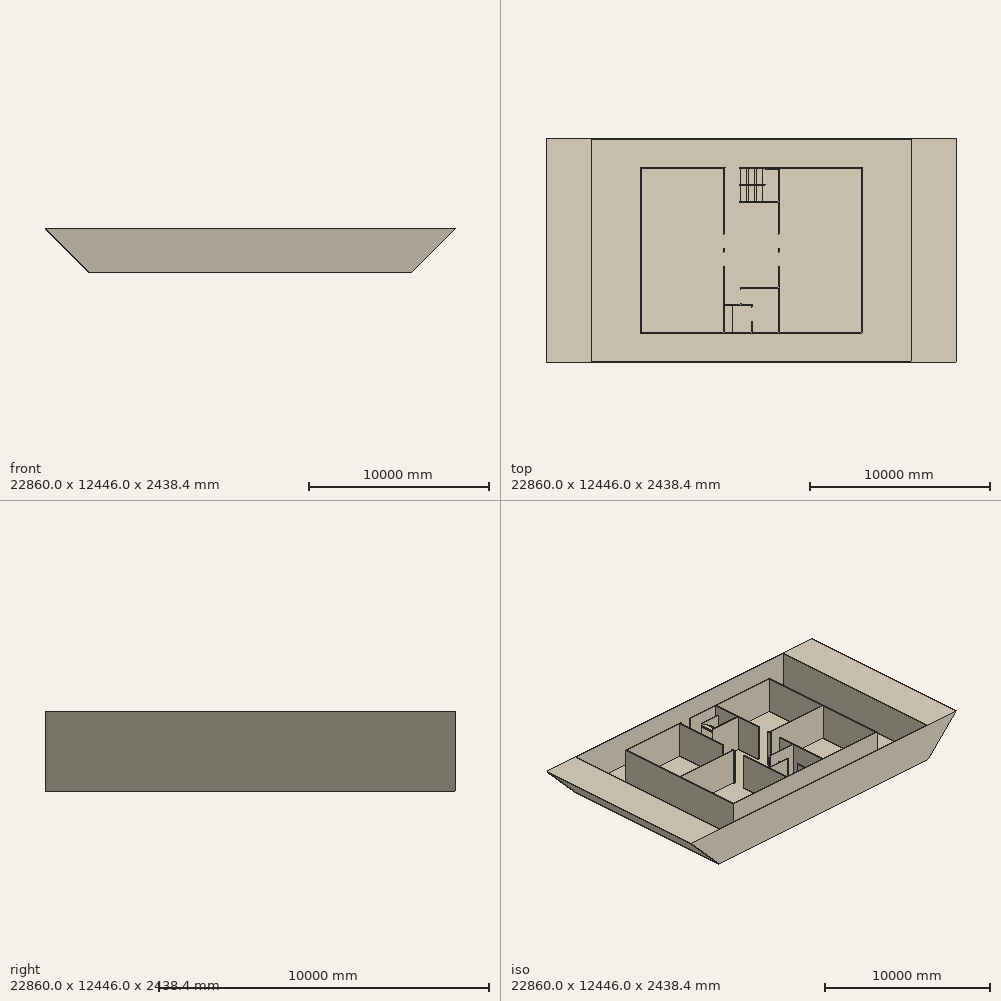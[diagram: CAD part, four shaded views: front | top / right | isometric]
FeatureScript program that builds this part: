
annotation { "Feature Type Name" : "Feature", "Feature Type Description" : "" }
export const myFeature = defineFeature(function(context is Context, id is Id, definition is map)
    precondition{}
    {
        {
            var Q0;
            Q0=qCreatedBy(makeId("Top.planeOp"),FACE);
            var sketch = newSketch(context, id + "F0", { "sketchPlane" : qUnion([Q0])});
            skLineSegment(sketch, "E0.bottom", {"start": v(-95.25, -51.86) * mm, "end": v(95.25, -51.86) * mm});
            skLineSegment(sketch, "E0.top", {"start": v(-95.25, 51.86) * mm, "end": v(95.25, 51.86) * mm});
            skLineSegment(sketch, "E0.left", {"start": v(-95.25, -51.86) * mm, "end": v(-95.25, 51.86) * mm});
            skLineSegment(sketch, "E0.right", {"start": v(95.25, -51.86) * mm, "end": v(95.25, 51.86) * mm});
            skPoint(sketch, "E0.middle", {"position": v(0, 0) * mm});
            skSolve(sketch);
        }
        {
            var Q0;
            Q0=makeQuery(id+"F0.imprint","IMPRINT",FACE,{"disambiguationData":[TD([[makeQuery(id+"F0.imprint","IMPRINT",EDGE,{"derivedFrom":sQuery(id+"F0.wireOp",EDGE,"E0.bottom")}),1.0]])]});
            extrude(context, id + "F1", {"entities" : qUnion([Q0]), "depth" : 20.32 * mm});
        }
        {
            var Q0;
            Q0=makeQuery(id+"F1.opExtrude","CAP_EDGE",EDGE,{"disambiguationData":[OSD([sQuery(id+"F0.wireOp",EDGE,"E0.right")])],"isStart":true});
            var Q1;
            Q1=makeQuery(id+"F1.opExtrude","CAP_EDGE",EDGE,{"disambiguationData":[OSD([sQuery(id+"F0.wireOp",EDGE,"E0.left")])],"isStart":true});
            chamfer(context, id + "F2", {"entities" : qUnion([Q0, Q1]), "width" : 20.32 * mm, "tangentPropagation" : true});
        }
        {
            var Q0;
            Q0=makeQuery(id+"F1.opExtrude","CAP_FACE",FACE,{"disambiguationData":[OSD([sQuery(id+"F0.wireOp",EDGE,"E0.bottom"),sQuery(id+"F0.wireOp",EDGE,"E0.top"),sQuery(id+"F0.wireOp",EDGE,"E0.left"),sQuery(id+"F0.wireOp",EDGE,"E0.right")])],"isStart":false});
            var sketch = newSketch(context, id + "F3", { "sketchPlane" : qUnion([Q0])});
            skLineSegment(sketch, "E1.bottom", {"start": v(-51.65, -38.73) * mm, "end": v(51.65, -38.73) * mm});
            skLineSegment(sketch, "E1.top", {"start": v(-51.65, 38.73) * mm, "end": v(51.65, 38.73) * mm});
            skLineSegment(sketch, "E1.left", {"start": v(-51.65, -38.73) * mm, "end": v(-51.65, 38.73) * mm});
            skLineSegment(sketch, "E1.right", {"start": v(51.65, -38.73) * mm, "end": v(51.65, 38.74) * mm});
            skPoint(sketch, "E1.middle", {"position": v(0, 0) * mm});
            skLineSegment(sketch, "E2.bottom", {"start": v(-74.5, -51.44) * mm, "end": v(74.5, -51.44) * mm});
            skLineSegment(sketch, "E2.top", {"start": v(-74.5, 51.44) * mm, "end": v(74.5, 51.44) * mm});
            skLineSegment(sketch, "E2.left", {"start": v(-74.5, -51.44) * mm, "end": v(-74.5, 51.44) * mm});
            skLineSegment(sketch, "E2.right", {"start": v(74.5, -51.44) * mm, "end": v(74.5, 51.44) * mm});
            skLineSegment(sketch, "E3", {"start": v(-74.93, 51.86) * mm, "end": v(-74.93, -51.86) * mm});
            skLineSegment(sketch, "E4", {"start": v(74.93, 51.86) * mm, "end": v(74.93, -51.86) * mm});
            skLineSegment(sketch, "E5.bottom", {"start": v(-51.22, 38.31) * mm, "end": v(-13.12, 38.31) * mm});
            skLineSegment(sketch, "E5.top", {"start": v(-51.22, 0.21) * mm, "end": v(-13.12, 0.21) * mm});
            skLineSegment(sketch, "E5.left", {"start": v(-51.22, 38.31) * mm, "end": v(-51.22, 0.21) * mm});
            skLineSegment(sketch, "E5.right", {"start": v(-13.12, 38.31) * mm, "end": v(-13.12, 0.21) * mm});
            skLineSegment(sketch, "E6.bottom", {"start": v(-51.22, -0.21) * mm, "end": v(-13.12, -0.21) * mm});
            skLineSegment(sketch, "E6.top", {"start": v(-51.22, -38.31) * mm, "end": v(-13.12, -38.31) * mm});
            skLineSegment(sketch, "E6.left", {"start": v(-51.22, -0.21) * mm, "end": v(-51.22, -38.31) * mm});
            skLineSegment(sketch, "E6.right", {"start": v(-13.12, -0.21) * mm, "end": v(-13.12, -38.31) * mm});
            skLineSegment(sketch, "E7.bottom", {"start": v(13.12, 38.31) * mm, "end": v(51.22, 38.31) * mm});
            skLineSegment(sketch, "E7.top", {"start": v(13.12, 0.21) * mm, "end": v(51.22, 0.21) * mm});
            skLineSegment(sketch, "E7.left", {"start": v(13.12, 38.31) * mm, "end": v(13.12, 0.21) * mm});
            skLineSegment(sketch, "E7.right", {"start": v(51.22, 38.31) * mm, "end": v(51.22, 0.21) * mm});
            skLineSegment(sketch, "E8.bottom", {"start": v(13.12, -0.21) * mm, "end": v(51.22, -0.21) * mm});
            skLineSegment(sketch, "E8.top", {"start": v(13.12, -38.31) * mm, "end": v(51.22, -38.31) * mm});
            skLineSegment(sketch, "E8.left", {"start": v(13.12, -0.21) * mm, "end": v(13.12, -38.31) * mm});
            skLineSegment(sketch, "E8.right", {"start": v(51.22, -0.21) * mm, "end": v(51.22, -38.31) * mm});
            skLineSegment(sketch, "E9", {"start": v(-12.7, 38.73) * mm, "end": v(-12.7, -38.74) * mm});
            skLineSegment(sketch, "E10", {"start": v(12.7, 38.73) * mm, "end": v(12.7, -38.74) * mm});
            skLineSegment(sketch, "E11", {"start": v(-12.7, 38.31) * mm, "end": v(12.7, 38.31) * mm});
            skLineSegment(sketch, "E12", {"start": v(12.7, -38.31) * mm, "end": v(-12.7, -38.31) * mm});
            skLineSegment(sketch, "E13", {"start": v(-12.7, -25.61) * mm, "end": v(0, -25.61) * mm});
            skLineSegment(sketch, "E14", {"start": v(-12.7, -17.14) * mm, "end": v(12.7, -17.14) * mm});
            skLineSegment(sketch, "E15", {"start": v(-12.7, -17.57) * mm, "end": v(12.7, -17.57) * mm});
            skLineSegment(sketch, "E16", {"start": v(-12.7, -25.19) * mm, "end": v(0, -25.19) * mm});
            skLineSegment(sketch, "E17", {"start": v(0, -25.19) * mm, "end": v(0, -25.61) * mm});
            skLineSegment(sketch, "E18", {"start": v(0, -25.61) * mm, "end": v(0, -38.31) * mm});
            skLineSegment(sketch, "E19", {"start": v(0.42, -38.31) * mm, "end": v(0.42, -25.19) * mm});
            skLineSegment(sketch, "E20", {"start": v(0.42, -25.19) * mm, "end": v(0, -25.19) * mm});
            skLineSegment(sketch, "E21", {"start": v(-5.08, -17.14) * mm, "end": v(-5.08, -25.19) * mm});
            skLineSegment(sketch, "E22", {"start": v(-4.66, -17.57) * mm, "end": v(-4.66, -25.19) * mm});
            skSolve(sketch);
        }
        {
            var Q0;
            {var subQ1=sQuery(id+"F3.wireOp",EDGE,"E1.left");Q0=makeQuery(id+"F3.imprint","IMPRINT",FACE,{"disambiguationData":[TD([[makeQuery(id+"F3.imprint","IMPRINT",EDGE,{"derivedFrom":subQ1}),1.0]])]});}
            var Q1;
            Q1=makeQuery(id+"F3.imprint","IMPRINT",FACE,{"disambiguationData":[TD([[makeQuery(id+"F3.imprint","IMPRINT",EDGE,{"derivedFrom":sQuery(id+"F3.wireOp",EDGE,"E5.bottom")}),-1.0]])]});
            var Q2;
            Q2=makeQuery(id+"F3.imprint","IMPRINT",FACE,{"disambiguationData":[TD([[makeQuery(id+"F3.imprint","IMPRINT",EDGE,{"derivedFrom":sQuery(id+"F3.wireOp",EDGE,"E6.bottom")}),-1.0]])]});
            var Q3;
            {var subQ0=sQuery(id+"F3.wireOp",EDGE,"E11");Q3=makeQuery(id+"F3.imprint","IMPRINT",FACE,{"disambiguationData":[TD([[makeQuery(id+"F3.imprint","IMPRINT",EDGE,{"derivedFrom":subQ0}),-1.0]])]});}
            var Q4;
            Q4=makeQuery(id+"F3.imprint","IMPRINT",FACE,{"disambiguationData":[TD([[makeQuery(id+"F3.imprint","IMPRINT",EDGE,{"derivedFrom":sQuery(id+"F3.wireOp",EDGE,"E7.bottom")}),-1.0]])]});
            var Q5;
            Q5=makeQuery(id+"F3.imprint","IMPRINT",FACE,{"disambiguationData":[TD([[makeQuery(id+"F3.imprint","IMPRINT",EDGE,{"derivedFrom":sQuery(id+"F3.wireOp",EDGE,"E8.bottom")}),-1.0]])]});
            var Q6;
            {var subQ0=sQuery(id+"F3.wireOp",EDGE,"E14");var subQ1=sQuery(id+"F3.wireOp",EDGE,"E9");var subQ2=makeQuery(id+"F3.imprint","INTERSECT",VERTEX,{"derivedFrom":[subQ1,subQ0]});Q6=makeQuery(id+"F3.imprint","IMPRINT",FACE,{"disambiguationData":[TD([[makeQuery(id+"F3.imprint","IMPRINT",EDGE,{"disambiguationData":[TD([[subQ2,-1.0]])],"derivedFrom":subQ1}),1.0]])]});}
            var Q7;
            {var subQ0=sQuery(id+"F3.wireOp",EDGE,"E15");var subQ1=sQuery(id+"F3.wireOp",EDGE,"E9");var subQ2=makeQuery(id+"F3.imprint","INTERSECT",VERTEX,{"derivedFrom":[subQ1,subQ0]});Q7=makeQuery(id+"F3.imprint","IMPRINT",FACE,{"disambiguationData":[TD([[makeQuery(id+"F3.imprint","IMPRINT",EDGE,{"disambiguationData":[TD([[subQ2,-1.0]])],"derivedFrom":subQ1}),1.0]])]});}
            var Q8;
            {var subQ3=sQuery(id+"F3.wireOp",EDGE,"E13");Q8=makeQuery(id+"F3.imprint","IMPRINT",FACE,{"disambiguationData":[TD([[makeQuery(id+"F3.imprint","IMPRINT",EDGE,{"derivedFrom":subQ3}),-1.0]])]});}
            var Q9;
            {var subQ7=sQuery(id+"F3.wireOp",EDGE,"E19");Q9=makeQuery(id+"F3.imprint","IMPRINT",FACE,{"disambiguationData":[TD([[makeQuery(id+"F3.imprint","IMPRINT",EDGE,{"derivedFrom":subQ7}),-1.0]])]});}
            extrude(context, id + "F4", {"entities" : qUnion([Q0, Q1, Q2, Q3, Q4, Q5, Q6, Q7, Q8, Q9]), "operationType" : NewBodyOperationType.REMOVE, "oppositeDirection" : true, "depth" : 19.05 * mm});
        }
        {
            var Q0;
            Q0=makeQuery(id+"F4.boolean.opBoolean","COPY",FACE,{"derivedFrom":makeQuery(id+"F4.opExtrude","CAP_FACE",FACE,{"disambiguationData":[OSD([sQuery(id+"F3.wireOp",EDGE,"E8.bottom"),sQuery(id+"F3.wireOp",EDGE,"E8.top"),sQuery(id+"F3.wireOp",EDGE,"E8.left"),sQuery(id+"F3.wireOp",EDGE,"E8.right")])],"isStart":false})});
            var sketch = newSketch(context, id + "F5", { "sketchPlane" : qUnion([Q0])});
            skLineSegment(sketch, "E23.bottom", {"start": v(-14.93, -1.06) * mm, "end": v(-4.43, -1.06) * mm});
            skLineSegment(sketch, "E23.top", {"start": v(-14.93, -7.4) * mm, "end": v(-4.43, -7.4) * mm});
            skLineSegment(sketch, "E23.left", {"start": v(-14.93, -1.06) * mm, "end": v(-14.93, -7.4) * mm});
            skLineSegment(sketch, "E23.right", {"start": v(-4.43, -1.06) * mm, "end": v(-4.43, -7.4) * mm});
            skLineSegment(sketch, "E24.bottom", {"start": v(4.64, -1.06) * mm, "end": v(13.64, -1.06) * mm});
            skLineSegment(sketch, "E24.top", {"start": v(4.64, -7.4) * mm, "end": v(13.64, -7.4) * mm});
            skLineSegment(sketch, "E24.left", {"start": v(4.64, -1.06) * mm, "end": v(4.64, -7.4) * mm});
            skLineSegment(sketch, "E24.right", {"start": v(13.64, -1.06) * mm, "end": v(13.64, -7.4) * mm});
            skLineSegment(sketch, "E25.bottom", {"start": v(13.6, 1.06) * mm, "end": v(2.84, 1.06) * mm});
            skLineSegment(sketch, "E25.top", {"start": v(13.6, 7.4) * mm, "end": v(2.84, 7.4) * mm});
            skLineSegment(sketch, "E25.left", {"start": v(13.6, 1.06) * mm, "end": v(13.6, 7.4) * mm});
            skLineSegment(sketch, "E25.right", {"start": v(2.84, 1.06) * mm, "end": v(2.84, 7.4) * mm});
            skLineSegment(sketch, "E26.bottom", {"start": v(-13.48, 7.4) * mm, "end": v(-3.4, 7.4) * mm});
            skLineSegment(sketch, "E26.top", {"start": v(-13.48, 1.06) * mm, "end": v(-3.4, 1.06) * mm});
            skLineSegment(sketch, "E26.left", {"start": v(-13.48, 7.4) * mm, "end": v(-13.48, 1.06) * mm});
            skLineSegment(sketch, "E26.right", {"start": v(-3.4, 7.4) * mm, "end": v(-3.4, 1.06) * mm});
            skLineSegment(sketch, "E27.bottom", {"start": v(-8.3, -18.2) * mm, "end": v(0, -18.2) * mm});
            skLineSegment(sketch, "E27.top", {"start": v(-8.3, -24.55) * mm, "end": v(0, -24.55) * mm});
            skLineSegment(sketch, "E27.left", {"start": v(-8.3, -18.2) * mm, "end": v(-8.3, -24.55) * mm});
            skLineSegment(sketch, "E27.right", {"start": v(0, -18.2) * mm, "end": v(0, -24.55) * mm});
            skLineSegment(sketch, "E28.bottom", {"start": v(-11.85, 42.33) * mm, "end": v(-5.5, 42.33) * mm});
            skLineSegment(sketch, "E28.top", {"start": v(-11.85, 34.48) * mm, "end": v(-5.5, 34.48) * mm});
            skLineSegment(sketch, "E28.left", {"start": v(-11.85, 42.33) * mm, "end": v(-11.85, 34.48) * mm});
            skLineSegment(sketch, "E28.right", {"start": v(-5.5, 42.33) * mm, "end": v(-5.5, 34.48) * mm});
            skLineSegment(sketch, "E29.bottom", {"start": v(-2.51, -26.46) * mm, "end": v(3, -26.46) * mm});
            skLineSegment(sketch, "E29.top", {"start": v(-2.51, -32.8) * mm, "end": v(3, -32.8) * mm});
            skLineSegment(sketch, "E29.left", {"start": v(-2.51, -26.46) * mm, "end": v(-2.51, -32.8) * mm});
            skLineSegment(sketch, "E29.right", {"start": v(3, -26.46) * mm, "end": v(3, -32.8) * mm});
            skSolve(sketch);
        }
        {
            var Q0;
            Q0 = qSketchRegion(id + "F5", true);
            extrude(context, id + "F6", {"entities" : qUnion([Q0]), "operationType" : NewBodyOperationType.REMOVE, "depth" : 25.4 * mm});
        }
        {
            var Q0;
            {var subQ0=sQuery(id+"F3.wireOp",EDGE,"E16");var subQ1=sQuery(id+"F3.wireOp",EDGE,"E10");Q0=makeQuery(id+"F6.boolean.opBoolean","MERGE",FACE,{"derivedFrom":[makeQuery(id+"F4.boolean.opBoolean","COPY",FACE,{"derivedFrom":makeQuery(id+"F4.opExtrude","CAP_FACE",FACE,{"disambiguationData":[OSD([sQuery(id+"F3.wireOp",EDGE,"E1.bottom"),sQuery(id+"F3.wireOp",EDGE,"E1.top"),sQuery(id+"F3.wireOp",EDGE,"E1.left"),sQuery(id+"F3.wireOp",EDGE,"E1.right"),sQuery(id+"F3.wireOp",EDGE,"E2.bottom"),sQuery(id+"F3.wireOp",EDGE,"E2.top"),sQuery(id+"F3.wireOp",EDGE,"E2.left"),sQuery(id+"F3.wireOp",EDGE,"E2.right")])],"isStart":false})}),makeQuery(id+"F4.boolean.opBoolean","COPY",FACE,{"derivedFrom":makeQuery(id+"F4.opExtrude","CAP_FACE",FACE,{"disambiguationData":[OSD([sQuery(id+"F3.wireOp",EDGE,"E5.bottom"),sQuery(id+"F3.wireOp",EDGE,"E5.top"),sQuery(id+"F3.wireOp",EDGE,"E5.left"),sQuery(id+"F3.wireOp",EDGE,"E5.right")])],"isStart":false})}),makeQuery(id+"F4.boolean.opBoolean","COPY",FACE,{"derivedFrom":makeQuery(id+"F4.opExtrude","CAP_FACE",FACE,{"disambiguationData":[OSD([sQuery(id+"F3.wireOp",EDGE,"E6.bottom"),sQuery(id+"F3.wireOp",EDGE,"E6.top"),sQuery(id+"F3.wireOp",EDGE,"E6.left"),sQuery(id+"F3.wireOp",EDGE,"E6.right")])],"isStart":false})}),makeQuery(id+"F4.boolean.opBoolean","COPY",FACE,{"derivedFrom":makeQuery(id+"F4.opExtrude","CAP_FACE",FACE,{"disambiguationData":[OSD([sQuery(id+"F3.wireOp",EDGE,"E7.bottom"),sQuery(id+"F3.wireOp",EDGE,"E7.top"),sQuery(id+"F3.wireOp",EDGE,"E7.left"),sQuery(id+"F3.wireOp",EDGE,"E7.right")])],"isStart":false})}),makeQuery(id+"F4.boolean.opBoolean","COPY",FACE,{"derivedFrom":makeQuery(id+"F4.opExtrude","CAP_FACE",FACE,{"disambiguationData":[OSD([sQuery(id+"F3.wireOp",EDGE,"E8.bottom"),sQuery(id+"F3.wireOp",EDGE,"E8.top"),sQuery(id+"F3.wireOp",EDGE,"E8.left"),sQuery(id+"F3.wireOp",EDGE,"E8.right")])],"isStart":false})}),makeQuery(id+"F4.boolean.opBoolean","COPY",FACE,{"derivedFrom":makeQuery(id+"F4.opExtrude","CAP_FACE",FACE,{"disambiguationData":[OSD([sQuery(id+"F3.wireOp",EDGE,"E9"),subQ1,sQuery(id+"F3.wireOp",EDGE,"E11"),sQuery(id+"F3.wireOp",EDGE,"E14"),subQ0,sQuery(id+"F3.wireOp",EDGE,"E21")])],"isStart":false})}),makeQuery(id+"F4.boolean.opBoolean","COPY",FACE,{"derivedFrom":makeQuery(id+"F4.opExtrude","CAP_FACE",FACE,{"disambiguationData":[OSD([subQ1,sQuery(id+"F3.wireOp",EDGE,"E12"),sQuery(id+"F3.wireOp",EDGE,"E15"),subQ0,sQuery(id+"F3.wireOp",EDGE,"E19"),sQuery(id+"F3.wireOp",EDGE,"E20"),sQuery(id+"F3.wireOp",EDGE,"E22")])],"isStart":false})}),makeQuery(id+"F6.opExtrude","CAP_FACE",FACE,{"disambiguationData":[OSD([sQuery(id+"F5.wireOp",EDGE,"E23.bottom"),sQuery(id+"F5.wireOp",EDGE,"E23.top"),sQuery(id+"F5.wireOp",EDGE,"E23.left"),sQuery(id+"F5.wireOp",EDGE,"E23.right")])],"isStart":true}),makeQuery(id+"F6.opExtrude","CAP_FACE",FACE,{"disambiguationData":[OSD([sQuery(id+"F5.wireOp",EDGE,"E24.bottom"),sQuery(id+"F5.wireOp",EDGE,"E24.top"),sQuery(id+"F5.wireOp",EDGE,"E24.left"),sQuery(id+"F5.wireOp",EDGE,"E24.right")])],"isStart":true}),makeQuery(id+"F6.opExtrude","CAP_FACE",FACE,{"disambiguationData":[OSD([sQuery(id+"F5.wireOp",EDGE,"E25.bottom"),sQuery(id+"F5.wireOp",EDGE,"E25.top"),sQuery(id+"F5.wireOp",EDGE,"E25.left"),sQuery(id+"F5.wireOp",EDGE,"E25.right")])],"isStart":true}),makeQuery(id+"F6.opExtrude","CAP_FACE",FACE,{"disambiguationData":[OSD([sQuery(id+"F5.wireOp",EDGE,"E26.bottom"),sQuery(id+"F5.wireOp",EDGE,"E26.top"),sQuery(id+"F5.wireOp",EDGE,"E26.left"),sQuery(id+"F5.wireOp",EDGE,"E26.right")])],"isStart":true}),makeQuery(id+"F6.opExtrude","CAP_FACE",FACE,{"disambiguationData":[OSD([sQuery(id+"F5.wireOp",EDGE,"E27.bottom"),sQuery(id+"F5.wireOp",EDGE,"E27.top"),sQuery(id+"F5.wireOp",EDGE,"E27.left"),sQuery(id+"F5.wireOp",EDGE,"E27.right")])],"isStart":true}),makeQuery(id+"F6.opExtrude","CAP_FACE",FACE,{"disambiguationData":[OSD([sQuery(id+"F5.wireOp",EDGE,"E28.bottom"),sQuery(id+"F5.wireOp",EDGE,"E28.top"),sQuery(id+"F5.wireOp",EDGE,"E28.left"),sQuery(id+"F5.wireOp",EDGE,"E28.right")])],"isStart":true})]});}
            var sketch = newSketch(context, id + "F7", { "sketchPlane" : qUnion([Q0])});
            skLineSegment(sketch, "E30", {"start": v(12.7, 30.7) * mm, "end": v(-5.5, 30.7) * mm});
            skLineSegment(sketch, "E31", {"start": v(12.7, 30.27) * mm, "end": v(-5.5, 30.27) * mm});
            skLineSegment(sketch, "E32", {"start": v(-5.5, 30.27) * mm, "end": v(-5.5, 30.7) * mm});
            skLineSegment(sketch, "E33", {"start": v(6.35, 30.7) * mm, "end": v(6.35, 30.27) * mm});
            skSolve(sketch);
        }
        {
            var Q0;
            {var subQ0=sQuery(id+"F7.wireOp",EDGE,"E32");Q0=makeQuery(id+"F7.imprint","IMPRINT",FACE,{"disambiguationData":[TD([[makeQuery(id+"F7.imprint","IMPRINT",EDGE,{"derivedFrom":subQ0}),-1.0]])]});}
            extrude(context, id + "F8", {"entities" : qUnion([Q0]), "operationType" : NewBodyOperationType.ADD, "depth" : 19.05 * mm});
        }
        {
            var Q0;
            Q0=makeQuery(id+"F4.boolean.opBoolean","COPY",FACE,{"derivedFrom":makeQuery(id+"F4.opExtrude","SWEPT_FACE",FACE,{"disambiguationData":[OSD([sQuery(id+"F3.wireOp",EDGE,"E11")])]})});
            var sketch = newSketch(context, id + "F9", { "sketchPlane" : qUnion([Q0])});
            skLineSegment(sketch, "E34.bottom", {"start": v(-5.08, 3.81) * mm, "end": v(-2.54, 3.81) * mm});
            skLineSegment(sketch, "E34.top", {"start": v(-5.08, 2.96) * mm, "end": v(-2.54, 2.96) * mm});
            skLineSegment(sketch, "E34.left", {"start": v(-5.08, 3.81) * mm, "end": v(-5.08, 2.96) * mm});
            skLineSegment(sketch, "E34.right", {"start": v(-2.54, 3.81) * mm, "end": v(-2.54, 2.96) * mm});
            skLineSegment(sketch, "E35.bottom", {"start": v(2.54, 8.9) * mm, "end": v(5.08, 8.9) * mm});
            skLineSegment(sketch, "E35.top", {"start": v(2.54, 8.04) * mm, "end": v(5.08, 8.04) * mm});
            skLineSegment(sketch, "E35.left", {"start": v(2.54, 8.9) * mm, "end": v(2.54, 8.04) * mm});
            skLineSegment(sketch, "E35.right", {"start": v(5.08, 8.9) * mm, "end": v(5.08, 8.04) * mm});
            skLineSegment(sketch, "E36.bottom", {"start": v(6.35, 11.43) * mm, "end": v(8.9, 11.43) * mm});
            skLineSegment(sketch, "E36.top", {"start": v(6.35, 10.58) * mm, "end": v(8.9, 10.58) * mm});
            skLineSegment(sketch, "E36.left", {"start": v(6.35, 11.43) * mm, "end": v(6.35, 10.58) * mm});
            skLineSegment(sketch, "E36.right", {"start": v(8.9, 11.43) * mm, "end": v(8.9, 10.58) * mm});
            skLineSegment(sketch, "E37.bottom", {"start": v(-1.27, 6.35) * mm, "end": v(1.27, 6.35) * mm});
            skLineSegment(sketch, "E37.top", {"start": v(-1.27, 5.5) * mm, "end": v(1.27, 5.5) * mm});
            skLineSegment(sketch, "E37.left", {"start": v(-1.27, 6.35) * mm, "end": v(-1.27, 5.5) * mm});
            skLineSegment(sketch, "E37.right", {"start": v(1.27, 6.35) * mm, "end": v(1.27, 5.5) * mm});
            skLineSegment(sketch, "E38.bottom", {"start": v(8.9, 11.43) * mm, "end": v(12.7, 11.43) * mm});
            skLineSegment(sketch, "E38.top", {"start": v(8.9, 10.58) * mm, "end": v(12.7, 10.58) * mm});
            skLineSegment(sketch, "E38.right", {"start": v(12.7, 11.43) * mm, "end": v(12.7, 10.58) * mm});
            skSolve(sketch);
        }
        {
            var Q0;
            Q0=makeQuery(id+"F9.imprint","IMPRINT",FACE,{"disambiguationData":[TD([[makeQuery(id+"F9.imprint","IMPRINT",EDGE,{"derivedFrom":sQuery(id+"F9.wireOp",EDGE,"E34.bottom")}),-1.0]])]});
            var Q1;
            Q1=makeQuery(id+"F9.imprint","IMPRINT",FACE,{"disambiguationData":[TD([[makeQuery(id+"F9.imprint","IMPRINT",EDGE,{"derivedFrom":sQuery(id+"F9.wireOp",EDGE,"E37.bottom")}),-1.0]])]});
            var Q2;
            Q2=makeQuery(id+"F9.imprint","IMPRINT",FACE,{"disambiguationData":[TD([[makeQuery(id+"F9.imprint","IMPRINT",EDGE,{"derivedFrom":sQuery(id+"F9.wireOp",EDGE,"E35.bottom")}),-1.0]])]});
            extrude(context, id + "F10", {"entities" : qUnion([Q0, Q1, Q2]), "operationType" : NewBodyOperationType.ADD, "depth" : 7.62 * mm});
        }
        {
            var Q0;
            Q0=makeQuery(id+"F9.imprint","IMPRINT",FACE,{"disambiguationData":[TD([[makeQuery(id+"F9.imprint","IMPRINT",EDGE,{"derivedFrom":sQuery(id+"F9.wireOp",EDGE,"E36.bottom")}),-1.0]])]});
            var Q1;
            Q1=makeQuery(id+"F9.imprint","IMPRINT",FACE,{"disambiguationData":[TD([[makeQuery(id+"F9.imprint","IMPRINT",EDGE,{"derivedFrom":sQuery(id+"F9.wireOp",EDGE,"E38.bottom")}),-1.0]])]});
            extrude(context, id + "F11", {"entities" : qUnion([Q0, Q1]), "operationType" : NewBodyOperationType.ADD, "depth" : (.6 + (.1 / 6)) * mm});
        }
        {
            var Q0;
            {var subQ0=sQuery(id+"F3.wireOp",EDGE,"E16");var subQ1=sQuery(id+"F3.wireOp",EDGE,"E10");Q0=makeQuery(id+"F6.boolean.opBoolean","MERGE",FACE,{"derivedFrom":[makeQuery(id+"F4.boolean.opBoolean","COPY",FACE,{"derivedFrom":makeQuery(id+"F4.opExtrude","CAP_FACE",FACE,{"disambiguationData":[OSD([sQuery(id+"F3.wireOp",EDGE,"E1.bottom"),sQuery(id+"F3.wireOp",EDGE,"E1.top"),sQuery(id+"F3.wireOp",EDGE,"E1.left"),sQuery(id+"F3.wireOp",EDGE,"E1.right"),sQuery(id+"F3.wireOp",EDGE,"E2.bottom"),sQuery(id+"F3.wireOp",EDGE,"E2.top"),sQuery(id+"F3.wireOp",EDGE,"E2.left"),sQuery(id+"F3.wireOp",EDGE,"E2.right")])],"isStart":false})}),makeQuery(id+"F4.boolean.opBoolean","COPY",FACE,{"derivedFrom":makeQuery(id+"F4.opExtrude","CAP_FACE",FACE,{"disambiguationData":[OSD([sQuery(id+"F3.wireOp",EDGE,"E5.bottom"),sQuery(id+"F3.wireOp",EDGE,"E5.top"),sQuery(id+"F3.wireOp",EDGE,"E5.left"),sQuery(id+"F3.wireOp",EDGE,"E5.right")])],"isStart":false})}),makeQuery(id+"F4.boolean.opBoolean","COPY",FACE,{"derivedFrom":makeQuery(id+"F4.opExtrude","CAP_FACE",FACE,{"disambiguationData":[OSD([sQuery(id+"F3.wireOp",EDGE,"E6.bottom"),sQuery(id+"F3.wireOp",EDGE,"E6.top"),sQuery(id+"F3.wireOp",EDGE,"E6.left"),sQuery(id+"F3.wireOp",EDGE,"E6.right")])],"isStart":false})}),makeQuery(id+"F4.boolean.opBoolean","COPY",FACE,{"derivedFrom":makeQuery(id+"F4.opExtrude","CAP_FACE",FACE,{"disambiguationData":[OSD([sQuery(id+"F3.wireOp",EDGE,"E7.bottom"),sQuery(id+"F3.wireOp",EDGE,"E7.top"),sQuery(id+"F3.wireOp",EDGE,"E7.left"),sQuery(id+"F3.wireOp",EDGE,"E7.right")])],"isStart":false})}),makeQuery(id+"F4.boolean.opBoolean","COPY",FACE,{"derivedFrom":makeQuery(id+"F4.opExtrude","CAP_FACE",FACE,{"disambiguationData":[OSD([sQuery(id+"F3.wireOp",EDGE,"E8.bottom"),sQuery(id+"F3.wireOp",EDGE,"E8.top"),sQuery(id+"F3.wireOp",EDGE,"E8.left"),sQuery(id+"F3.wireOp",EDGE,"E8.right")])],"isStart":false})}),makeQuery(id+"F4.boolean.opBoolean","COPY",FACE,{"derivedFrom":makeQuery(id+"F4.opExtrude","CAP_FACE",FACE,{"disambiguationData":[OSD([sQuery(id+"F3.wireOp",EDGE,"E9"),subQ1,sQuery(id+"F3.wireOp",EDGE,"E11"),sQuery(id+"F3.wireOp",EDGE,"E14"),subQ0,sQuery(id+"F3.wireOp",EDGE,"E21")])],"isStart":false})}),makeQuery(id+"F4.boolean.opBoolean","COPY",FACE,{"derivedFrom":makeQuery(id+"F4.opExtrude","CAP_FACE",FACE,{"disambiguationData":[OSD([subQ1,sQuery(id+"F3.wireOp",EDGE,"E12"),sQuery(id+"F3.wireOp",EDGE,"E15"),subQ0,sQuery(id+"F3.wireOp",EDGE,"E19"),sQuery(id+"F3.wireOp",EDGE,"E20"),sQuery(id+"F3.wireOp",EDGE,"E22")])],"isStart":false})}),makeQuery(id+"F6.opExtrude","CAP_FACE",FACE,{"disambiguationData":[OSD([sQuery(id+"F5.wireOp",EDGE,"E23.bottom"),sQuery(id+"F5.wireOp",EDGE,"E23.top"),sQuery(id+"F5.wireOp",EDGE,"E23.left"),sQuery(id+"F5.wireOp",EDGE,"E23.right")])],"isStart":true}),makeQuery(id+"F6.opExtrude","CAP_FACE",FACE,{"disambiguationData":[OSD([sQuery(id+"F5.wireOp",EDGE,"E24.bottom"),sQuery(id+"F5.wireOp",EDGE,"E24.top"),sQuery(id+"F5.wireOp",EDGE,"E24.left"),sQuery(id+"F5.wireOp",EDGE,"E24.right")])],"isStart":true}),makeQuery(id+"F6.opExtrude","CAP_FACE",FACE,{"disambiguationData":[OSD([sQuery(id+"F5.wireOp",EDGE,"E25.bottom"),sQuery(id+"F5.wireOp",EDGE,"E25.top"),sQuery(id+"F5.wireOp",EDGE,"E25.left"),sQuery(id+"F5.wireOp",EDGE,"E25.right")])],"isStart":true}),makeQuery(id+"F6.opExtrude","CAP_FACE",FACE,{"disambiguationData":[OSD([sQuery(id+"F5.wireOp",EDGE,"E26.bottom"),sQuery(id+"F5.wireOp",EDGE,"E26.top"),sQuery(id+"F5.wireOp",EDGE,"E26.left"),sQuery(id+"F5.wireOp",EDGE,"E26.right")])],"isStart":true}),makeQuery(id+"F6.opExtrude","CAP_FACE",FACE,{"disambiguationData":[OSD([sQuery(id+"F5.wireOp",EDGE,"E27.bottom"),sQuery(id+"F5.wireOp",EDGE,"E27.top"),sQuery(id+"F5.wireOp",EDGE,"E27.left"),sQuery(id+"F5.wireOp",EDGE,"E27.right")])],"isStart":true}),makeQuery(id+"F6.opExtrude","CAP_FACE",FACE,{"disambiguationData":[OSD([sQuery(id+"F5.wireOp",EDGE,"E28.bottom"),sQuery(id+"F5.wireOp",EDGE,"E28.top"),sQuery(id+"F5.wireOp",EDGE,"E28.left"),sQuery(id+"F5.wireOp",EDGE,"E28.right")])],"isStart":true})]});}
            var sketch = newSketch(context, id + "F12", { "sketchPlane" : qUnion([Q0])});
            skLineSegment(sketch, "E39.bottom", {"start": v(12.7, 22.65) * mm, "end": v(-5.5, 22.65) * mm});
            skLineSegment(sketch, "E39.top", {"start": v(12.7, 22.22) * mm, "end": v(-5.5, 22.22) * mm});
            skLineSegment(sketch, "E39.left", {"start": v(12.7, 22.65) * mm, "end": v(12.7, 22.22) * mm});
            skLineSegment(sketch, "E39.right", {"start": v(-5.5, 22.65) * mm, "end": v(-5.5, 22.22) * mm});
            skSolve(sketch);
        }
        {
            var Q0;
            Q0 = qSketchRegion(id + "F12", true);
            extrude(context, id + "F13", {"entities" : qUnion([Q0]), "operationType" : NewBodyOperationType.ADD, "depth" : 19.05 * mm});
        }
        {
            var Q0;
            Q0=makeQuery(id+"F8.opExtrude","SWEPT_FACE",FACE,{"disambiguationData":[OSD([sQuery(id+"F7.wireOp",EDGE,"E31")])]});
            var sketch = newSketch(context, id + "F14", { "sketchPlane" : qUnion([Q0])});
            skLineSegment(sketch, "E40.bottom", {"start": v(-1.27, 16.51) * mm, "end": v(1.27, 16.51) * mm});
            skLineSegment(sketch, "E40.top", {"start": v(-1.27, 15.66) * mm, "end": v(1.27, 15.66) * mm});
            skLineSegment(sketch, "E40.left", {"start": v(-1.27, 16.51) * mm, "end": v(-1.27, 15.66) * mm});
            skLineSegment(sketch, "E40.right", {"start": v(1.27, 16.51) * mm, "end": v(1.27, 15.66) * mm});
            skLineSegment(sketch, "E41.bottom", {"start": v(5.08, 13.97) * mm, "end": v(2.54, 13.97) * mm});
            skLineSegment(sketch, "E41.top", {"start": v(5.08, 12.95) * mm, "end": v(2.54, 12.95) * mm});
            skLineSegment(sketch, "E41.left", {"start": v(5.08, 13.97) * mm, "end": v(5.08, 12.95) * mm});
            skLineSegment(sketch, "E41.right", {"start": v(2.54, 13.97) * mm, "end": v(2.54, 12.95) * mm});
            skLineSegment(sketch, "E42.bottom", {"start": v(-2.54, 19.05) * mm, "end": v(-5.08, 19.05) * mm});
            skLineSegment(sketch, "E42.top", {"start": v(-2.54, 18.2) * mm, "end": v(-5.08, 18.2) * mm});
            skLineSegment(sketch, "E42.left", {"start": v(-2.54, 19.05) * mm, "end": v(-2.54, 18.2) * mm});
            skLineSegment(sketch, "E42.right", {"start": v(-5.08, 19.05) * mm, "end": v(-5.08, 18.2) * mm});
            skSolve(sketch);
        }
        {
            var Q0;
            Q0 = qSketchRegion(id + "F14", true);
            extrude(context, id + "F15", {"entities" : qUnion([Q0]), "operationType" : NewBodyOperationType.ADD, "depth" : 7.62 * mm});
        }
        {
            var Q0;
            Q0=makeQuery(id+"F4.boolean.opBoolean","COPY",FACE,{"derivedFrom":makeQuery(id+"F4.opExtrude","CAP_FACE",FACE,{"disambiguationData":[OSD([sQuery(id+"F3.wireOp",EDGE,"E9"),sQuery(id+"F3.wireOp",EDGE,"E12"),sQuery(id+"F3.wireOp",EDGE,"E13"),sQuery(id+"F3.wireOp",EDGE,"E18")])],"isStart":false})});
            var sketch = newSketch(context, id + "F16", { "sketchPlane" : qUnion([Q0])});
            skLineSegment(sketch, "E43.bottom", {"start": v(-12.7, -25.61) * mm, "end": v(-8.89, -25.61) * mm});
            skLineSegment(sketch, "E43.top", {"start": v(-12.7, -38.31) * mm, "end": v(-8.89, -38.31) * mm});
            skLineSegment(sketch, "E43.left", {"start": v(-12.7, -25.61) * mm, "end": v(-12.7, -38.31) * mm});
            skLineSegment(sketch, "E43.right", {"start": v(-8.89, -25.61) * mm, "end": v(-8.89, -38.31) * mm});
            skSolve(sketch);
        }
        {
            var Q0;
            Q0 = qSketchRegion(id + "F16", true);
            extrude(context, id + "F17", {"entities" : qUnion([Q0]), "operationType" : NewBodyOperationType.ADD, "depth" : 3.8 * mm});
        }
        {
            var Q0;
            Q0=makeQuery(id+"F1.opExtrude","SWEPT_BODY",BODY,{"disambiguationData":[OSD([sQuery(id+"F0.wireOp",EDGE,"E0.bottom"),sQuery(id+"F0.wireOp",EDGE,"E0.top"),sQuery(id+"F0.wireOp",EDGE,"E0.left"),sQuery(id+"F0.wireOp",EDGE,"E0.right")])]});
            var Q1;
            Q1=qCreatedBy(makeId("Origin.pointOp"),VERTEX);
            transform(context, id + "F18", {"entities" : qUnion([Q0]), "transformType" : TransformType.SCALE_UNIFORMLY, "scale" : 12, "scalePoint" : qUnion([Q1]), "makeCopy" : false});
        }
        {
            var Q0;
            Q0=makeQuery(id+"F1.opExtrude","SWEPT_BODY",BODY,{"disambiguationData":[OSD([sQuery(id+"F0.wireOp",EDGE,"E0.bottom"),sQuery(id+"F0.wireOp",EDGE,"E0.top"),sQuery(id+"F0.wireOp",EDGE,"E0.left"),sQuery(id+"F0.wireOp",EDGE,"E0.right")])]});
            var Q1;
            Q1=qCreatedBy(makeId("Origin.pointOp"),VERTEX);
            transform(context, id + "F19", {"entities" : qUnion([Q0]), "transformType" : TransformType.SCALE_UNIFORMLY, "scale" : 10, "scalePoint" : qUnion([Q1]), "makeCopy" : false});
        }
    });
